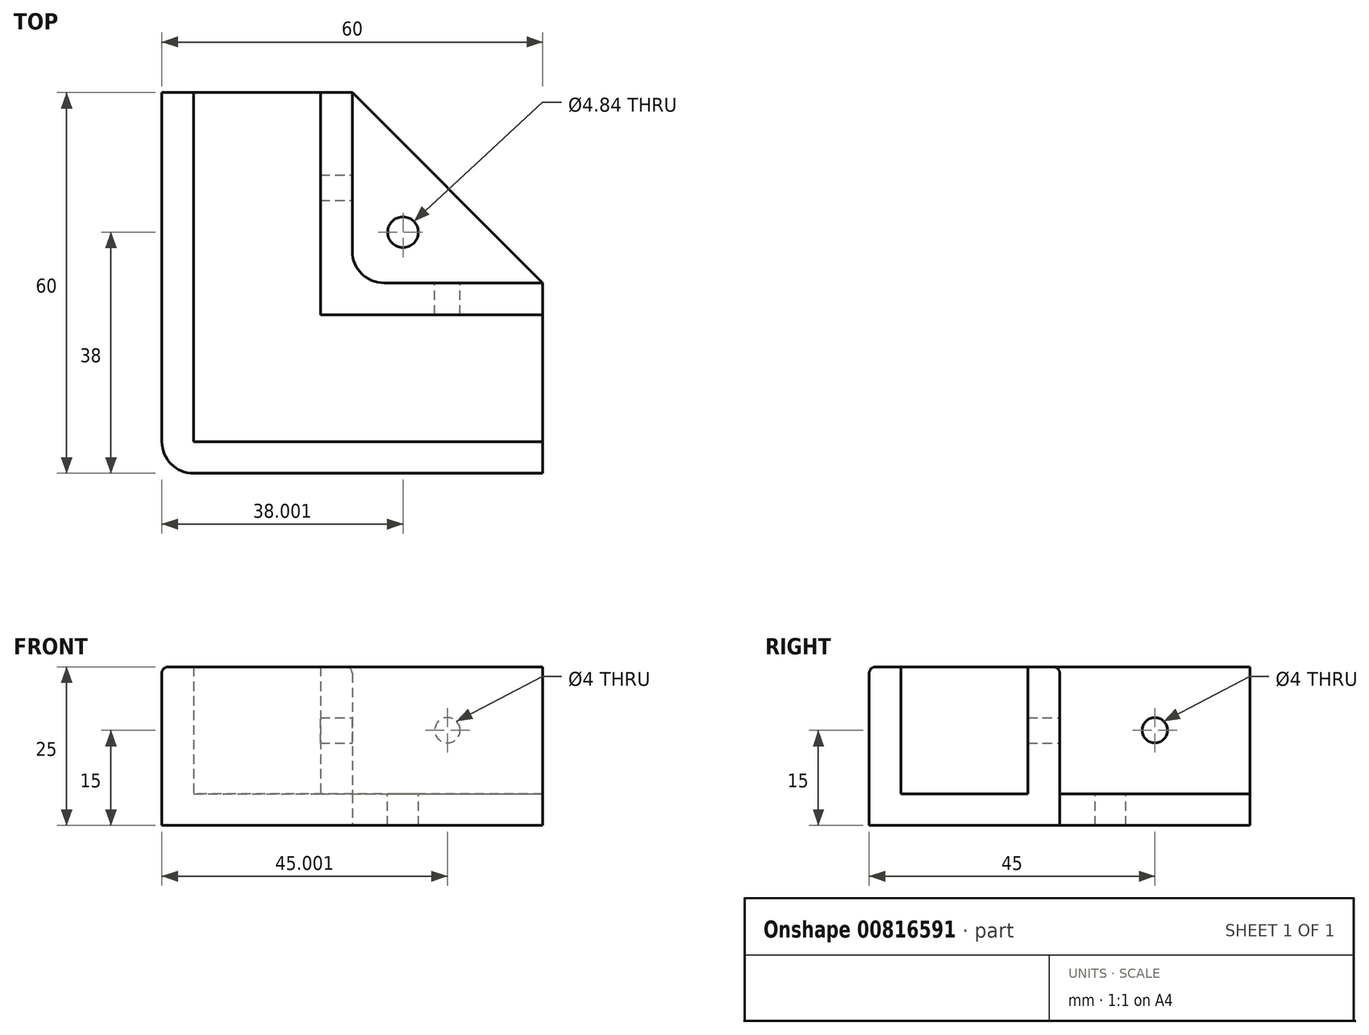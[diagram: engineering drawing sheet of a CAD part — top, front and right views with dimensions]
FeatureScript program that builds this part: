
annotation { "Feature Type Name" : "Feature", "Feature Type Description" : "" }
export const myFeature = defineFeature(function(context is Context, id is Id, definition is map)
    precondition{}
    {
        {
            var Q0;
            Q0=qCreatedBy(makeId("Top.planeOp"),FACE);
            var sketch = newSketch(context, id + "F0", { "sketchPlane" : qUnion([Q0])});
            skLineSegment(sketch, "E0", {"start": v(-53.43, 30) * mm, "end": v(-23.43, 30) * mm});
            skLineSegment(sketch, "E1", {"start": v(6.57, 0) * mm, "end": v(6.57, -30) * mm});
            skLineSegment(sketch, "E2", {"start": v(6.57, -30) * mm, "end": v(-53.43, -30) * mm});
            skLineSegment(sketch, "E3", {"start": v(-53.43, -30) * mm, "end": v(-53.43, 30) * mm});
            skLineSegment(sketch, "E4", {"start": v(6.57, 0) * mm, "end": v(-23.43, 30) * mm});
            skSolve(sketch);
        }
        {
            var Q0;
            Q0=makeQuery(id+"F0.imprint","IMPRINT",FACE,{"disambiguationData":[TD([[makeQuery(id+"F0.imprint","IMPRINT",EDGE,{"derivedFrom":sQuery(id+"F0.wireOp",EDGE,"E0")}),-1.0]])]});
            extrude(context, id + "F1", {"entities" : qUnion([Q0]), "depth" : 5 * mm, "offsetDistance" : 25 * mm});
        }
        {
            var Q0;
            Q0=makeQuery(id+"F1.opExtrude","CAP_FACE",FACE,{"disambiguationData":[OSD([sQuery(id+"F0.wireOp",EDGE,"E0"),sQuery(id+"F0.wireOp",EDGE,"JM1LwH4U-WR8i-0Fha-7gNJ-sKuIxwcslrcp"),sQuery(id+"F0.wireOp",EDGE,"GE3eAB2y-qTbw-y6U9-Kb9J-lxQVfWXzxVvi"),sQuery(id+"F0.wireOp",EDGE,"E1"),sQuery(id+"F0.wireOp",EDGE,"E2"),sQuery(id+"F0.wireOp",EDGE,"E3")])],"isStart":false});
            var sketch = newSketch(context, id + "F2", { "sketchPlane" : qUnion([Q0])});
            skLineSegment(sketch, "E5.0", {"start": v(-28.43, -5) * mm, "end": v(6.57, -5) * mm});
            skLineSegment(sketch, "E5.1", {"start": v(-28.43, 30) * mm, "end": v(-28.43, -5) * mm});
            skLineSegment(sketch, "E6.0", {"start": v(-48.43, -25) * mm, "end": v(-48.43, 30) * mm});
            skLineSegment(sketch, "E6.1", {"start": v(6.57, -25) * mm, "end": v(-48.43, -25) * mm});
            skLineSegment(sketch, "E7", {"start": v(-23.43, 30) * mm, "end": v(-23.43, 0) * mm});
            skLineSegment(sketch, "E8", {"start": v(-23.43, 0) * mm, "end": v(6.57, 0) * mm});
            skSolve(sketch);
        }
        {
            var Q0;
            {var subQ3=sQuery(id+"F2.wireOp",EDGE,"E6.0");Q0=makeQuery(id+"F2.imprint","IMPRINT",FACE,{"disambiguationData":[TD([[makeQuery(id+"F2.imprint","IMPRINT",EDGE,{"derivedFrom":subQ3}),1.0]])]});}
            var Q1;
            {var subQ3=sQuery(id+"F2.wireOp",EDGE,"E5.0");Q1=makeQuery(id+"F2.imprint","IMPRINT",FACE,{"disambiguationData":[TD([[makeQuery(id+"F2.imprint","IMPRINT",EDGE,{"derivedFrom":subQ3}),1.0]])]});}
            extrude(context, id + "F3", {"entities" : qUnion([Q0, Q1]), "operationType" : NewBodyOperationType.ADD, "depth" : 20 * mm, "offsetDistance" : 25 * mm});
        }
        {
            var Q0;
            Q0=makeQuery(id+"F3.opExtrude","SWEPT_FACE",FACE,{"disambiguationData":[OSD([sQuery(id+"F2.wireOp",EDGE,"E7")])]});
            var sketch = newSketch(context, id + "F4", { "sketchPlane" : qUnion([Q0])});
            skCircle(sketch, "E9", {"center": v(15, 15) * mm, "radius": 2 * mm});
            skLineSegment(sketch, "E10", {"start": v(0, 15) * mm, "end": v(30, 15) * mm, "construction": true});
            skSolve(sketch);
        }
        {
            var Q0;
            Q0=makeQuery(id+"F3.opExtrude","SWEPT_FACE",FACE,{"disambiguationData":[OSD([sQuery(id+"F2.wireOp",EDGE,"E8")])]});
            var sketch = newSketch(context, id + "F5", { "sketchPlane" : qUnion([Q0])});
            skLineSegment(sketch, "E11", {"start": v(-6.57, 15) * mm, "end": v(23.43, 15) * mm, "construction": true});
            skCircle(sketch, "E12", {"center": v(8.43, 15) * mm, "radius": 2 * mm});
            skSolve(sketch);
        }
        {
            var Q0;
            {var subQ1=sQuery(id+"F0.wireOp",EDGE,"E4");var subQ2=sQuery(id+"F0.wireOp",EDGE,"E1");var subQ4=sQuery(id+"F0.wireOp",EDGE,"E0");var subQ7=sQuery(id+"F0.wireOp",EDGE,"E3");var subQ9=sQuery(id+"F0.wireOp",EDGE,"E2");Q0=makeQuery(id+"F3.boolean.opBoolean","SPLIT",FACE,{"disambiguationData":[TD([makeQuery(id+"F1.opExtrude","SWEPT_FACE",FACE,{"disambiguationData":[OSD([subQ1])]})])],"derivedFrom":makeQuery(id+"F1.opExtrude","CAP_FACE",FACE,{"disambiguationData":[OSD([subQ4,subQ2,subQ9,subQ7,subQ1])],"isStart":false})});}
            var sketch = newSketch(context, id + "F6", { "sketchPlane" : qUnion([Q0])});
            skCircle(sketch, "E13", {"center": v(-15.43, 8) * mm, "radius": 2.42 * mm});
            skSolve(sketch);
        }
        {
            var Q0;
            Q0=makeQuery(id+"F6.imprint","IMPRINT",FACE,{"disambiguationData":[TD([[makeQuery(id+"F6.imprint","IMPRINT",EDGE,{"derivedFrom":sQuery(id+"F6.wireOp",EDGE,"E13")}),1.0]])]});
            extrude(context, id + "F7", {"entities" : qUnion([Q0]), "operationType" : NewBodyOperationType.REMOVE, "oppositeDirection" : true, "depth" : 25 * mm, "offsetDistance" : 25 * mm});
        }
        {
            var Q0;
            Q0=makeQuery(id+"F3.opExtrude","SWEPT_EDGE",EDGE,{"disambiguationData":[OSD([sQuery(id+"F2.wireOp",EDGE,"E7"),sQuery(id+"F2.wireOp",EDGE,"E8")])]});
            fillet(context, id + "F8", {"entities" : qUnion([Q0]), "radius" : 5 * mm, "tangentPropagation" : true, "allowEdgeOverflow" : false});
        }
        {
            var Q0;
            {var subQ0=sQuery(id+"F0.wireOp",EDGE,"E3");var subQ1=sQuery(id+"F0.wireOp",EDGE,"E2");Q0=makeQuery(id+"F3.boolean.opBoolean","MERGE",EDGE,{"derivedFrom":[makeQuery(id+"F1.opExtrude","SWEPT_EDGE",EDGE,{"disambiguationData":[OSD([subQ1,subQ0])]}),makeQuery(id+"F3.opExtrude","SWEPT_EDGE",EDGE,{"disambiguationData":[OSD([subQ1,subQ0])]})]});}
            fillet(context, id + "F9", {"entities" : qUnion([Q0]), "radius" : 5 * mm, "tangentPropagation" : true, "allowEdgeOverflow" : false});
        }
        {
            var Q0;
            Q0=makeQuery(id+"F3.opExtrude","CAP_EDGE",EDGE,{"disambiguationData":[OSD([sQuery(id+"F0.wireOp",EDGE,"E2")])],"isStart":false});
            var Q1;
            Q1=makeQuery(id+"F3.opExtrude","CAP_EDGE",EDGE,{"disambiguationData":[OSD([sQuery(id+"F2.wireOp",EDGE,"E7")])],"isStart":false});
            fillet(context, id + "F10", {"entities" : qUnion([Q0, Q1]), "radius" : 1 * mm, "tangentPropagation" : true, "allowEdgeOverflow" : false});
        }
        {
            var Q0;
            {var subQ0=sQuery(id+"F4.wireOp",EDGE,"sEOiA8NR-tS9J-vnHA-3lF8-MbunqwK0pUbZ");var subQ4=makeQuery(id+"F4.imprint","INTERSECT",VERTEX,{"derivedFrom":[subQ0,sQuery(id+"F4.wireOp",EDGE,"I1mZ33px-Uupu-BQ1g-z2YM-ABmtIRaOaHo3")]});Q0=makeQuery(id+"F4.imprint","IMPRINT",FACE,{"disambiguationData":[TD([[makeQuery(id+"F4.imprint","IMPRINT",EDGE,{"disambiguationData":[TD([[subQ4,-1.0]])],"derivedFrom":subQ0}),1.0]])]});}
            var Q1;
            {var subQ0=sQuery(id+"F4.wireOp",EDGE,"sEOiA8NR-tS9J-vnHA-3lF8-MbunqwK0pUbZ");var subQ4=makeQuery(id+"F4.imprint","INTERSECT",VERTEX,{"derivedFrom":[subQ0,sQuery(id+"F4.wireOp",EDGE,"vQ90eD7C-S9mU-iYci-Ntlb-CJOyrzNFgVih")]});Q1=makeQuery(id+"F4.imprint","IMPRINT",FACE,{"disambiguationData":[TD([[makeQuery(id+"F4.imprint","IMPRINT",EDGE,{"disambiguationData":[TD([[subQ4,1.0]])],"derivedFrom":subQ0}),1.0]])]});}
            var Q2;
            {var subQ0=sQuery(id+"F4.wireOp",EDGE,"E9");var subQ4=makeQuery(id+"F4.imprint","INTERSECT",VERTEX,{"derivedFrom":[subQ0,sQuery(id+"F4.wireOp",EDGE,"vQ90eD7C-S9mU-iYci-Ntlb-CJOyrzNFgVih")]});Q2=makeQuery(id+"F4.imprint","IMPRINT",FACE,{"disambiguationData":[TD([[makeQuery(id+"F4.imprint","IMPRINT",EDGE,{"disambiguationData":[TD([[subQ4,-1.0]])],"derivedFrom":subQ0}),1.0]])]});}
            var Q3;
            {var subQ0=sQuery(id+"F4.wireOp",EDGE,"E9");var subQ4=makeQuery(id+"F4.imprint","INTERSECT",VERTEX,{"derivedFrom":[subQ0,sQuery(id+"F4.wireOp",EDGE,"I1mZ33px-Uupu-BQ1g-z2YM-ABmtIRaOaHo3")]});Q3=makeQuery(id+"F4.imprint","IMPRINT",FACE,{"disambiguationData":[TD([[makeQuery(id+"F4.imprint","IMPRINT",EDGE,{"disambiguationData":[TD([[subQ4,1.0]])],"derivedFrom":subQ0}),1.0]])]});}
            var Q4;
            {var subQ0=sQuery(id+"F4.wireOp",EDGE,"vQ90eD7C-S9mU-iYci-Ntlb-CJOyrzNFgVih");Q4=makeQuery(id+"F4.imprint","IMPRINT",FACE,{"disambiguationData":[TD([[makeQuery(id+"F4.imprint","IMPRINT",EDGE,{"derivedFrom":subQ0}),-1.0]])]});}
            var Q5;
            {var subQ0=sQuery(id+"F4.wireOp",EDGE,"I1mZ33px-Uupu-BQ1g-z2YM-ABmtIRaOaHo3");Q5=makeQuery(id+"F4.imprint","IMPRINT",FACE,{"disambiguationData":[TD([[makeQuery(id+"F4.imprint","IMPRINT",EDGE,{"derivedFrom":subQ0}),1.0]])]});}
            extrude(context, id + "F11", {"entities" : qUnion([Q0, Q1, Q2, Q3, Q4, Q5]), "operationType" : NewBodyOperationType.REMOVE, "oppositeDirection" : true, "depth" : 10 * mm, "offsetDistance" : 25 * mm});
        }
        {
            var Q0;
            {var subQ0=sQuery(id+"F5.wireOp",EDGE,"hI9UmZnd-uAhO-GbiI-mXmq-JLr7IBHHlGXU");var subQ1=makeQuery(id+"F5.imprint","INTERSECT",VERTEX,{"derivedFrom":[subQ0,sQuery(id+"F5.wireOp",EDGE,"o4Ciya7F-CI9P-Fl7D-Mul8-AiX0PgmwZnF6")]});Q0=makeQuery(id+"F5.imprint","IMPRINT",FACE,{"disambiguationData":[TD([[makeQuery(id+"F5.imprint","IMPRINT",EDGE,{"disambiguationData":[TD([[subQ1,1.0]])],"derivedFrom":subQ0}),1.0]])]});}
            var Q1;
            {var subQ0=sQuery(id+"F5.wireOp",EDGE,"E12");var subQ1=makeQuery(id+"F5.imprint","INTERSECT",VERTEX,{"derivedFrom":[subQ0,sQuery(id+"F5.wireOp",EDGE,"o4Ciya7F-CI9P-Fl7D-Mul8-AiX0PgmwZnF6")]});Q1=makeQuery(id+"F5.imprint","IMPRINT",FACE,{"disambiguationData":[TD([[makeQuery(id+"F5.imprint","IMPRINT",EDGE,{"disambiguationData":[TD([[subQ1,-1.0]])],"derivedFrom":subQ0}),1.0]])]});}
            var Q2;
            {var subQ0=sQuery(id+"F5.wireOp",EDGE,"m19K2vx0-NvKo-vfJp-d8cy-w1dIE6Jeab8T");Q2=makeQuery(id+"F5.imprint","IMPRINT",FACE,{"disambiguationData":[TD([[makeQuery(id+"F5.imprint","IMPRINT",EDGE,{"derivedFrom":subQ0}),1.0]])]});}
            var Q3;
            {var subQ0=sQuery(id+"F5.wireOp",EDGE,"o4Ciya7F-CI9P-Fl7D-Mul8-AiX0PgmwZnF6");Q3=makeQuery(id+"F5.imprint","IMPRINT",FACE,{"disambiguationData":[TD([[makeQuery(id+"F5.imprint","IMPRINT",EDGE,{"derivedFrom":subQ0}),-1.0]])]});}
            var Q4;
            {var subQ0=sQuery(id+"F5.wireOp",EDGE,"hI9UmZnd-uAhO-GbiI-mXmq-JLr7IBHHlGXU");var subQ1=sQuery(id+"F5.wireOp",EDGE,"E12");var subQ2=makeQuery(id+"F5.imprint","INTERSECT",VERTEX,{"disambiguationData":[OD(0.0)],"derivedFrom":[subQ1,subQ0]});Q4=makeQuery(id+"F5.imprint","IMPRINT",FACE,{"disambiguationData":[TD([[makeQuery(id+"F5.imprint","IMPRINT",EDGE,{"disambiguationData":[TD([[subQ2,-1.0]])],"derivedFrom":subQ1}),1.0]])]});}
            extrude(context, id + "F12", {"entities" : qUnion([Q0, Q1, Q2, Q3, Q4]), "operationType" : NewBodyOperationType.REMOVE, "oppositeDirection" : true, "depth" : 10 * mm, "offsetDistance" : 25 * mm});
        }
    });
